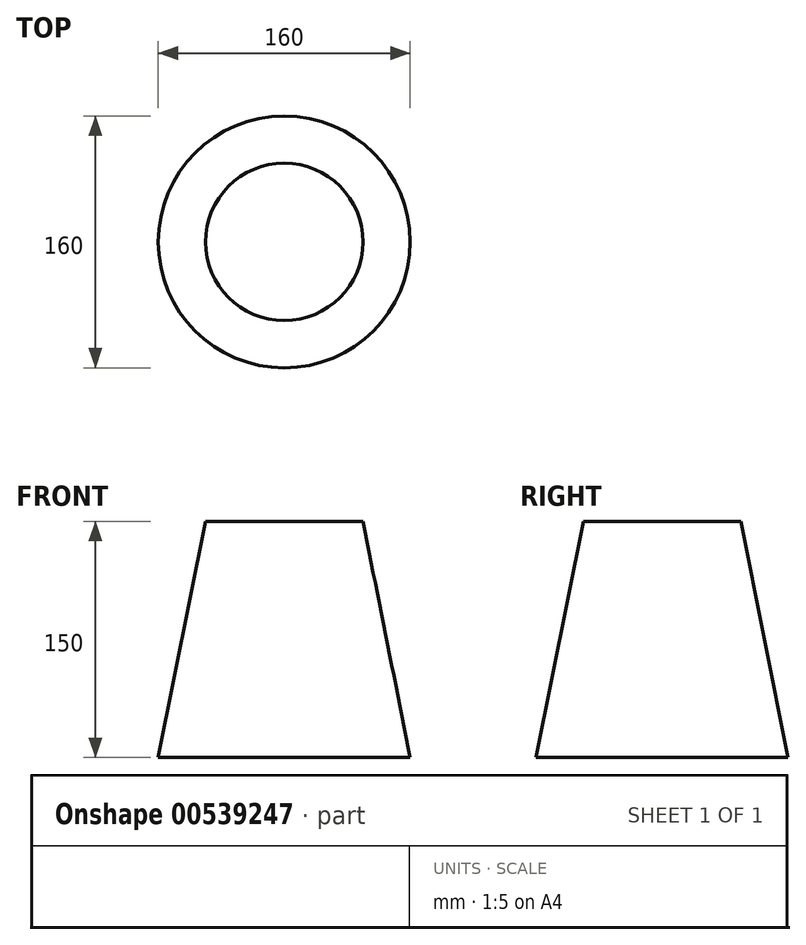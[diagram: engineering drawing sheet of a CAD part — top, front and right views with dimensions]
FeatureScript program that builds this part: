
annotation { "Feature Type Name" : "Feature", "Feature Type Description" : "" }
export const myFeature = defineFeature(function(context is Context, id is Id, definition is map)
    precondition{}
    {
        {
            var Q0;
            Q0=qCreatedBy(makeId("Top.planeOp"),FACE);
            var sketch = newSketch(context, id + "F0", { "sketchPlane" : qUnion([Q0])});
            skCircle(sketch, "E0", {"center": v(0, 0) * mm, "radius": 80 * mm});
            skSolve(sketch);
        }
        {
            var Q0;
            Q0=qCreatedBy(makeId("Top.planeOp"),FACE);
            cPlane(context, id + "F1", {"entities" : qUnion([Q0]), "cplaneType" : CPlaneType.OFFSET, "offset" : 150 * mm, "width" : 150 * mm, "height" : 150 * mm});
        }
        {
            var Q0;
            Q0=qCreatedBy(id+"F1.planeOp",FACE);
            var sketch = newSketch(context, id + "F2", { "sketchPlane" : qUnion([Q0])});
            skCircle(sketch, "E1", {"center": v(0, 0) * mm, "radius": 50 * mm});
            skSolve(sketch);
        }
        {
            var Q0;
            Q0=sQuery(id+"F0.wireOp",EDGE,"E0");
            var Q1;
            Q1=sQuery(id+"F2.wireOp",EDGE,"E1");
            loft(context, id + "F3", {"bodyType" : ToolBodyType.SURFACE, "wireProfilesArray" : [{ "wireProfileEntities" : qUnion([Q0]) }, { "wireProfileEntities" : qUnion([Q1]) }]});
        }
    });
